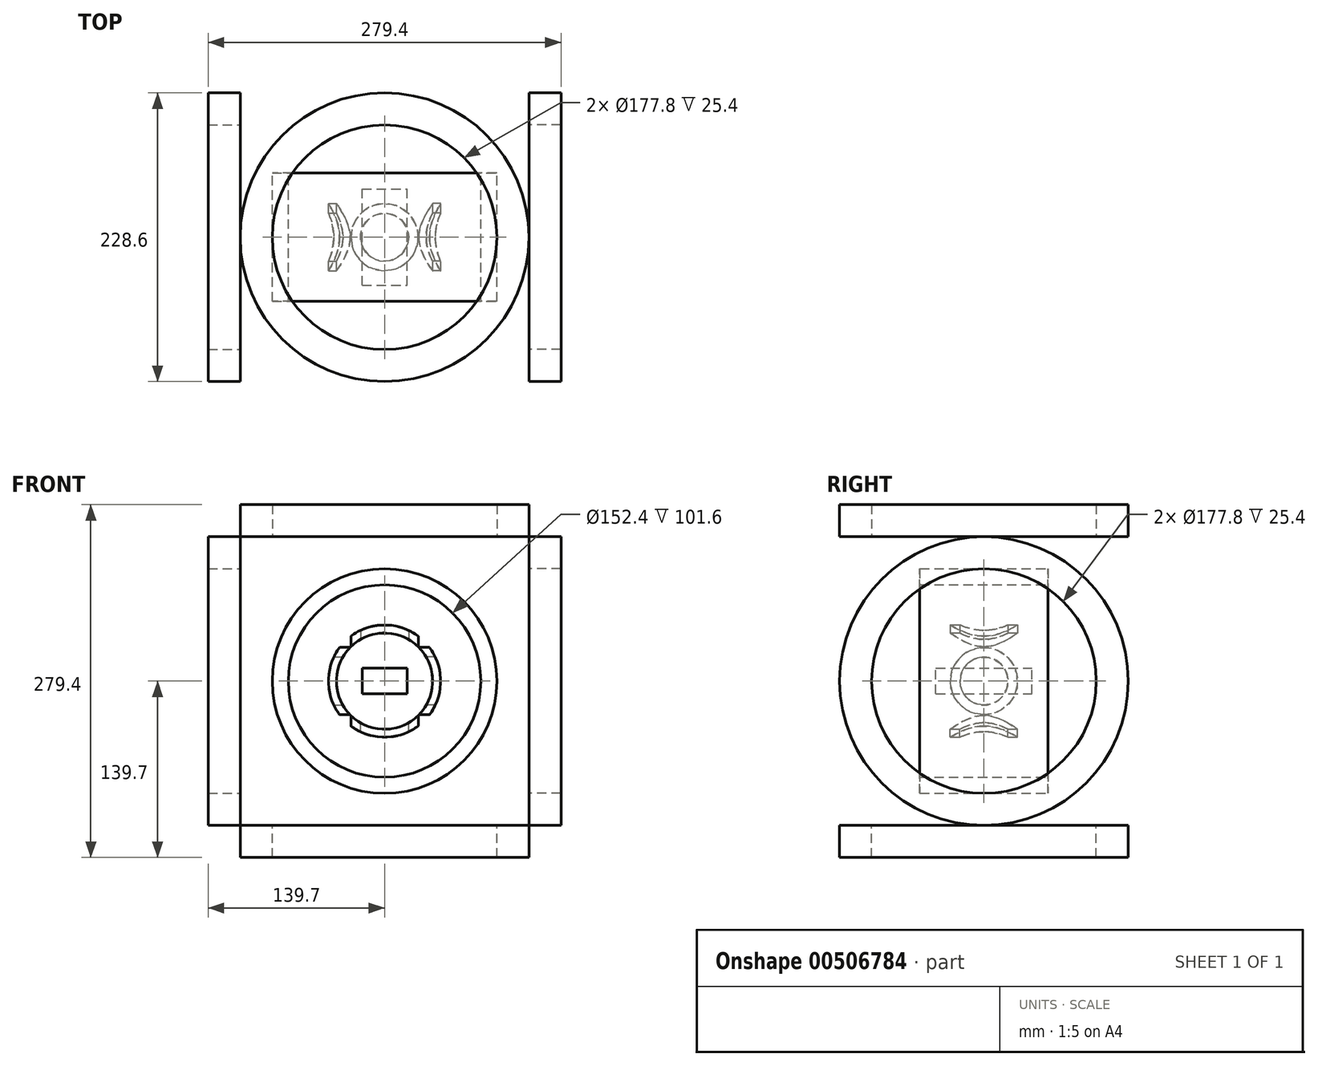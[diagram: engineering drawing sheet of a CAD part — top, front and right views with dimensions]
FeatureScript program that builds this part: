
annotation { "Feature Type Name" : "Feature", "Feature Type Description" : "" }
export const myFeature = defineFeature(function(context is Context, id is Id, definition is map)
    precondition{}
    {
        {
            var Q0;
            Q0=qCreatedBy(makeId("Front.planeOp"),FACE);
            var sketch = newSketch(context, id + "F0", { "sketchPlane" : qUnion([Q0])});
            skCircle(sketch, "E0", {"center": v(0, 0) * mm, "radius": 44.45 * mm});
            skCircle(sketch, "E1", {"center": v(0, 0) * mm, "radius": 38.1 * mm});
            skSolve(sketch);
        }
        {
            var Q0;
            Q0=makeQuery(id+"F0.imprint","IMPRINT",FACE,{"disambiguationData":[TD([[makeQuery(id+"F0.imprint","IMPRINT",EDGE,{"derivedFrom":sQuery(id+"F0.wireOp",EDGE,"E0")}),1.0]])]});
            extrude(context, id + "F1", {"entities" : qUnion([Q0]), "endBound" : BoundingType.SYMMETRIC, "offsetDistance" : 25.4 * mm, "depth" : 101.6 * mm});
        }
        {
            var Q0;
            Q0=qCreatedBy(makeId("Front.planeOp"),FACE);
            var sketch = newSketch(context, id + "F2", { "sketchPlane" : qUnion([Q0])});
            skLineSegment(sketch, "E2.bottom", {"start": v(-17.78, -10.16) * mm, "end": v(17.78, -10.16) * mm});
            skLineSegment(sketch, "E2.top", {"start": v(-17.78, 10.16) * mm, "end": v(17.78, 10.16) * mm});
            skLineSegment(sketch, "E2.left", {"start": v(-17.78, -10.16) * mm, "end": v(-17.78, 10.16) * mm});
            skLineSegment(sketch, "E2.right", {"start": v(17.78, -10.16) * mm, "end": v(17.78, 10.16) * mm});
            skSolve(sketch);
        }
        {
            var Q0;
            Q0 = qSketchRegion(id + "F2", true);
            var Q1;
            Q1=makeQuery(id+"F1.opExtrude","CAP_FACE",FACE,{"disambiguationData":[OSD([sQuery(id+"F0.wireOp",EDGE,"E0"),sQuery(id+"F0.wireOp",EDGE,"E1")])],"isStart":false});
            var Q2;
            Q2=makeQuery(id+"F1.opExtrude","CAP_FACE",FACE,{"disambiguationData":[OSD([sQuery(id+"F0.wireOp",EDGE,"E0"),sQuery(id+"F0.wireOp",EDGE,"E1")])],"isStart":true});
            extrude(context, id + "F3", {"entities" : qUnion([Q0]), "endBound" : BoundingType.UP_TO_SURFACE, "depth" : 25.4 * mm, "endBoundEntityFace" : qUnion([Q1]), "hasOffset" : true, "offsetDistance" : 12.7 * mm, "hasSecondDirection" : true, "secondDirectionBound" : SecondDirectionBoundingType.UP_TO_SURFACE, "secondDirectionOppositeDirection" : true, "secondDirectionDepth" : 25.4 * mm, "secondDirectionBoundEntityFace" : qUnion([Q2]), "hasSecondDirectionOffset" : true, "secondDirectionOffsetDistance" : 12.7 * mm});
        }
        {
            var Q0;
            Q0=qCreatedBy(makeId("Right.planeOp"),FACE);
            var sketch = newSketch(context, id + "F4", { "sketchPlane" : qUnion([Q0])});
            skCircle(sketch, "E3", {"center": v(0, 0) * mm, "radius": 26.67 * mm});
            skCircle(sketch, "E4", {"center": v(0, 0) * mm, "radius": 19.05 * mm});
            skSolve(sketch);
        }
        {
            var Q0;
            Q0=makeQuery(id+"F4.imprint","IMPRINT",FACE,{"disambiguationData":[TD([[makeQuery(id+"F4.imprint","IMPRINT",EDGE,{"derivedFrom":sQuery(id+"F4.wireOp",EDGE,"E3")}),1.0]])]});
            extrude(context, id + "F5", {"entities" : qUnion([Q0]), "depth" : 76.2 * mm, "offsetDistance" : 25.4 * mm});
        }
        {
            var Q0;
            Q0=makeQuery(id+"F1.opExtrude","SWEPT_BODY",BODY,{"disambiguationData":[OSD([sQuery(id+"F0.wireOp",EDGE,"E0"),sQuery(id+"F0.wireOp",EDGE,"E1")])]});
            var Q1;
            Q1=makeQuery(id+"F5.opExtrude","SWEPT_BODY",BODY,{"disambiguationData":[OSD([sQuery(id+"F4.wireOp",EDGE,"E3"),sQuery(id+"F4.wireOp",EDGE,"E4")])]});
            booleanBodies(context, id + "F6", {"operationType" : BooleanOperationType.INTERSECTION, "tools" : qUnion([Q0, Q1])});
        }
        {
            var Q0;
            Q0=qCreatedBy(makeId("Right.planeOp"),FACE);
            var sketch = newSketch(context, id + "F7", { "sketchPlane" : qUnion([Q0])});
            skLineSegment(sketch, "E5", {"start": v(0, 0) * mm, "end": v(-133.96, 0) * mm});
            skSolve(sketch);
        }
        {
            var Q0;
            Q0=makeQuery(id+"F6.opBoolean","INTERSECT",BODY,{"derivedFrom":[makeQuery(id+"F1.opExtrude","SWEPT_BODY",BODY,{"disambiguationData":[OSD([sQuery(id+"F0.wireOp",EDGE,"E0"),sQuery(id+"F0.wireOp",EDGE,"E1")])]}),makeQuery(id+"F5.opExtrude","SWEPT_BODY",BODY,{"disambiguationData":[OSD([sQuery(id+"F4.wireOp",EDGE,"E3"),sQuery(id+"F4.wireOp",EDGE,"E4")])]})]});
            var Q1;
            Q1=sQuery(id+"F7.wireOp",EDGE,"E5");
            circularPattern(context, id + "F8", {"entities" : qUnion([Q0]), "axis" : qUnion([Q1]), "angle" : 360 * degree, "instanceCount" : 4, "equalSpace" : true});
        }
        {
            var Q0;
            Q0=qCreatedBy(makeId("Front.planeOp"),FACE);
            var sketch = newSketch(context, id + "F9", { "sketchPlane" : qUnion([Q0])});
            skCircle(sketch, "E6", {"center": v(0, 0) * mm, "radius": 76.2 * mm});
            skCircle(sketch, "E7", {"center": v(0, 0) * mm, "radius": 88.9 * mm});
            skSolve(sketch);
        }
        {
            var Q0;
            Q0=makeQuery(id+"F9.imprint","IMPRINT",FACE,{"disambiguationData":[TD([[makeQuery(id+"F9.imprint","IMPRINT",EDGE,{"derivedFrom":sQuery(id+"F9.wireOp",EDGE,"E6")}),-1.0]])]});
            extrude(context, id + "F10", {"entities" : qUnion([Q0]), "endBound" : BoundingType.SYMMETRIC, "depth" : 101.6 * mm, "offsetDistance" : 25.4 * mm});
        }
        {
            var Q0;
            Q0=qCreatedBy(makeId("Right.planeOp"),FACE);
            cPlane(context, id + "F11", {"entities" : qUnion([Q0]), "cplaneType" : CPlaneType.OFFSET, "offset" : 127 * mm, "width" : 152.4 * mm, "height" : 152.4 * mm});
        }
        {
            var Q0;
            Q0=qCreatedBy(id+"F11.planeOp",FACE);
            var sketch = newSketch(context, id + "F12", { "sketchPlane" : qUnion([Q0])});
            skCircle(sketch, "E8", {"center": v(0, 0) * mm, "radius": 88.9 * mm});
            skCircle(sketch, "E9", {"center": v(0, 0) * mm, "radius": 114.3 * mm});
            skSolve(sketch);
        }
        {
            var Q0;
            Q0 = qSketchRegion(id + "F12", true);
            extrude(context, id + "F13", {"entities" : qUnion([Q0]), "endBound" : BoundingType.SYMMETRIC, "depth" : 25.4 * mm, "offsetDistance" : 25.4 * mm});
        }
        {
            var Q0;
            Q0=makeQuery(id+"F13.opExtrude","SWEPT_BODY",BODY,{"disambiguationData":[OSD([sQuery(id+"F12.wireOp",EDGE,"E8"),sQuery(id+"F12.wireOp",EDGE,"E9")])]});
            var Q1;
            Q1=sQuery(id+"F7.wireOp",EDGE,"E5");
            circularPattern(context, id + "F14", {"entities" : qUnion([Q0]), "axis" : qUnion([Q1]), "angle" : 360 * degree, "instanceCount" : 4, "equalSpace" : true});
        }
    });
